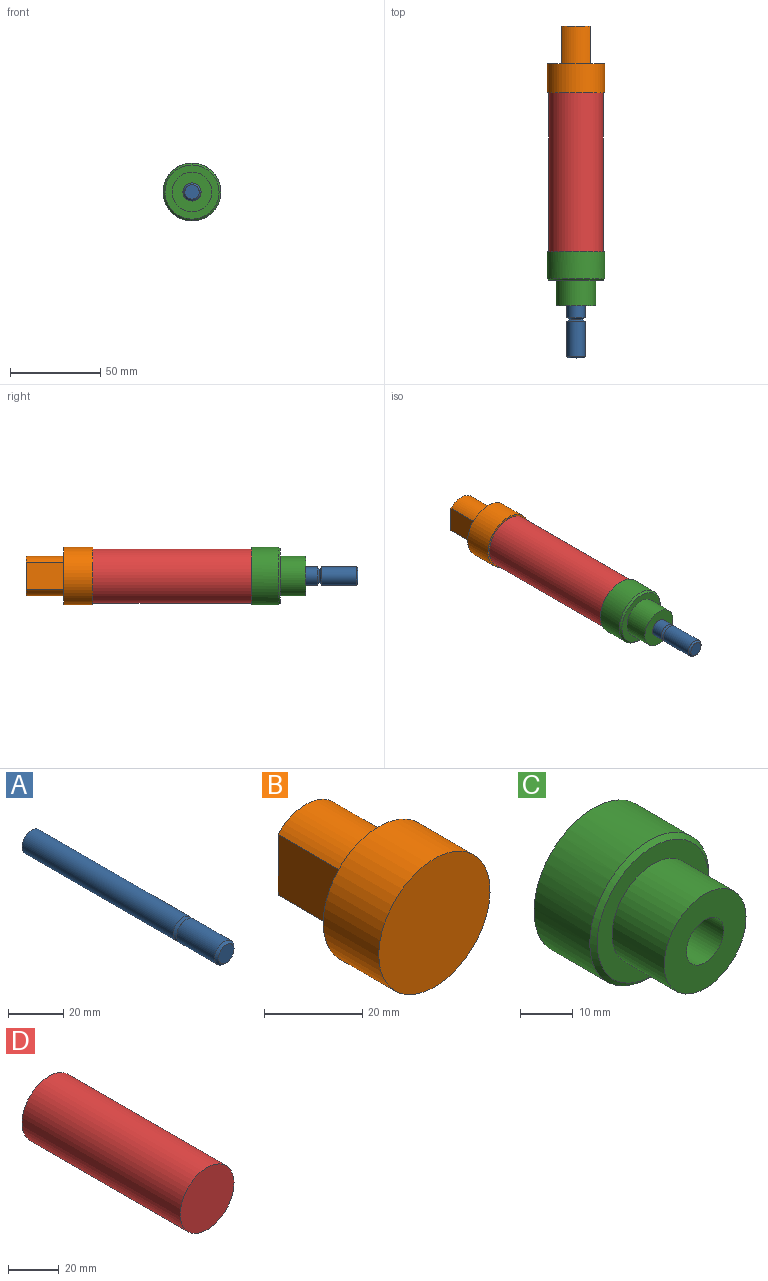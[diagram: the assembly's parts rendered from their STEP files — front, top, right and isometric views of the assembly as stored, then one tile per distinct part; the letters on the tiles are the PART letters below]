
ASSEMBLY  parts=4 mates=3
PART A: 7 faces, bbox 10x100x10 mm
  f0: cylinder r=5mm len=19.47mm, axis (0,-1,0), area 611.6mm2, adj f2,f6
  f1: plane 8x8mm, normal (0,-1,0), area 50.3mm2, adj f6
  f2: cone r=8.3mm half-angle=54.7deg, axis (0,-1,0), area 44.4mm2, adj f0,f3
  f3: cone r=3.67mm half-angle=55.7deg, axis (0,1,0), area 43.9mm2, adj f2,f5
  f4: plane 10x10mm, normal (0,1,0), area 78.5mm2, adj f5
  f5: cylinder r=5mm len=77.69mm, axis (0,-1,0), area 2440.5mm2, adj f3,f4
  f6: cone r=4mm half-angle=45deg, axis (0,1,0), area 40mm2, adj f0,f1
PART B: 8 faces, bbox 32x37x32 mm
  f0: plane 22x16mm, normal (0,1,0), area 317.9mm2, adj f1,f2,f6,f7
  f1: cylinder r=11mm len=21mm, axis (0,1,0), area 376.2mm2, adj f0,f4,f6,f7
  f2: cylinder r=11mm len=21mm, axis (0,1,0), area 376.2mm2, adj f0,f4,f6,f7
  f3: plane 32x32mm, normal (0,-1,0), area 804.2mm2, adj f5
  f4: plane 32x32mm, normal (0,1,0), area 486.4mm2, adj f1,f2,f5,f6,f7
  f5: cylinder r=16mm len=32mm, axis (0,1,0), area 1608.5mm2, adj f3,f4
  f6: plane 21x15.1mm, normal (1,0,0), area 317.1mm2, adj f0,f1,f2,f4
  f7: plane 21x15.1mm, normal (-1,0,0), area 317.1mm2, adj f0,f1,f2,f4
PART C: 7 faces, bbox 32x30x32 mm
  f0: plane 32x32mm, normal (0,1,0), area 725.7mm2, adj f1,f5
  f1: cylinder r=16mm len=32mm, axis (0,-1,0), area 1508mm2, adj f0,f6
  f2: plane 30x30mm, normal (0,-1,0), area 326.7mm2, adj f3,f6
  f3: cylinder r=11mm len=22mm, axis (0,-1,0), area 967.6mm2, adj f2,f4
  f4: plane 22x22mm, normal (0,-1,0), area 301.6mm2, adj f3,f5
  f5: cylinder r=5mm len=30mm, axis (0,-1,0), area 942.5mm2, adj f0,f4
  f6: cone r=15mm half-angle=45deg, axis (0,1,0), area 137.7mm2, adj f1,f2
PART D: 3 faces, bbox 30x88x30 mm
  f0: plane 29.97x29.97mm, normal (0,1,0), area 705.4mm2, adj f1
  f1: cylinder r=14.98mm len=88mm, axis (0,-1,0), area 8285mm2, adj f0,f2
  f2: plane 29.97x29.97mm, normal (0,-1,0), area 705.4mm2, adj f1
PLACE A t=(0,-59,0)mm
PLACE B t=(0,-60,0)mm
PLACE C t=(0,-60,0)mm
PLACE D t=(0,-60,0)mm
MATE fastened C.f1 <-> D.f1  axis (0,1,0) through (0,-44,0)mm
MATE fastened B.f1 <-> D.f1  axis (0,-1,0) through (0,44,0)mm
MATE slider A.f0 <-> C.f1  axis (0,-1,0) through (0,-102,0)mm
